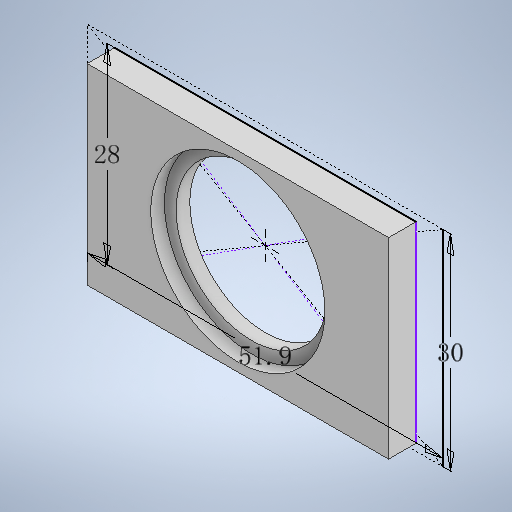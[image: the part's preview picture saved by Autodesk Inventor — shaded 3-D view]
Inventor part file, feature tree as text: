
AUTODESK INVENTOR PART (.ipt)
format: ipt  version: 2025 (Build 290162000, 162)  size: 267,776 bytes
history: native  units: mm
features: sketch x2, hole x2, extrude x1
ambient origin geometry x8: Origin, YZ Plane, XZ Plane, XY Plane, X Axis, Y Axis, Z Axis, Center Point
bodies: 实体1 (feature_tree)
feature tree (5):
  sketch  "草图1"  dims[d0=51.9mm d1=30.0mm]
  extrude  "拉伸1"  Depth=30.0mm
  hole  "孔1"  [1 undecoded]
  hole  "孔2"  [1 undecoded]
  sketch  "草图2"  dims[d6=28.0mm d7=4.0mm d8=0.0mm d9=4.95mm d10=6.0mm d11=4.0mm d12=2.0mm d13=90.0deg d14=2.5mm d15=20.594885mm d16=22.0mm d17=6.0mm d18=25.4mm d19=2.0mm d20=90.0deg d21=0.5mm d22=20.594885mm d23=1.0mm d24=1.0mm d25=1.0mm d26=0.15mm d27=0.25mm d28=0.375mm d29=14.3117mm d30=0.75mm d31=20.594885mm d32=0.0625mm d33=0.75mm d34=0.375mm d35=0.375mm]
note: 2 required parameter values undecoded (feature->parameter linkage not recoverable at this tier; creation-order binding heuristic only, values carry confidence <= 0.55)
